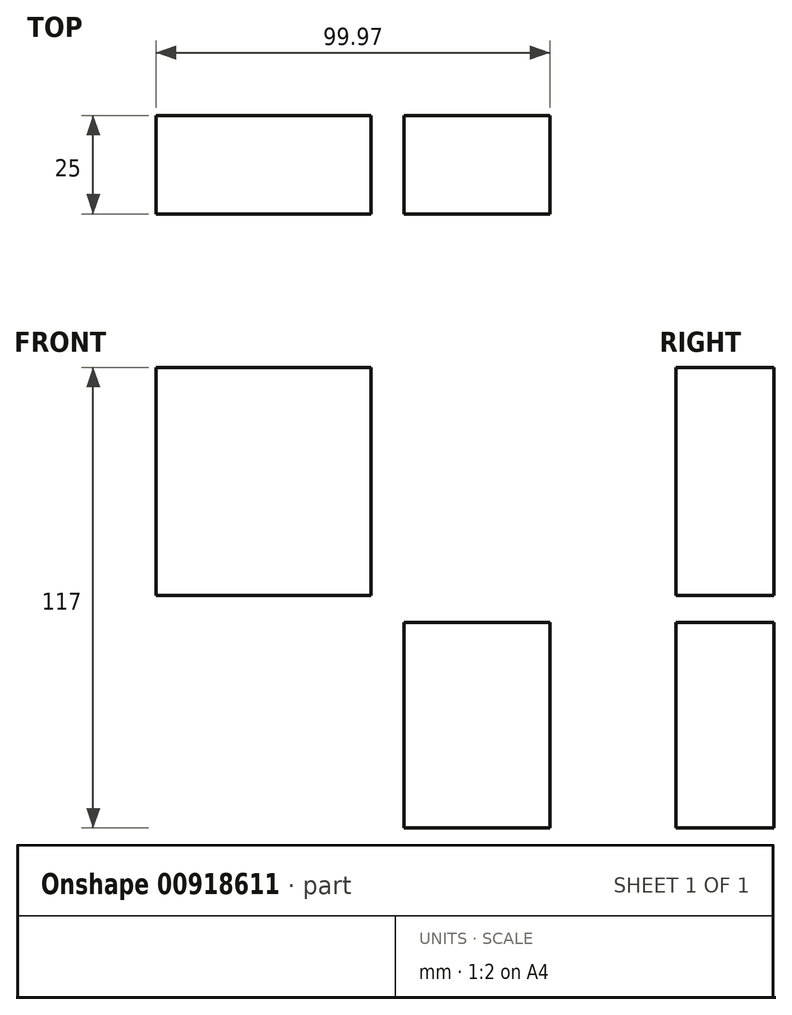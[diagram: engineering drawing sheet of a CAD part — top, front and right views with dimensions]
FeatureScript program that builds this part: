
annotation { "Feature Type Name" : "Feature", "Feature Type Description" : "" }
export const myFeature = defineFeature(function(context is Context, id is Id, definition is map)
    precondition{}
    {
        {
            var Q0;
            Q0=qCreatedBy(makeId("Front.planeOp"),FACE);
            var sketch = newSketch(context, id + "F0", { "sketchPlane" : qUnion([Q0])});
            skLineSegment(sketch, "E0.bottom", {"start": v(-133.56, 5.75) * mm, "end": v(-79.03, 5.75) * mm});
            skLineSegment(sketch, "E0.top", {"start": v(-133.56, 63.68) * mm, "end": v(-79.03, 63.68) * mm});
            skLineSegment(sketch, "E0.left", {"start": v(-133.56, 5.75) * mm, "end": v(-133.56, 63.68) * mm});
            skLineSegment(sketch, "E0.right", {"start": v(-79.03, 5.75) * mm, "end": v(-79.03, 63.68) * mm});
            skPoint(sketch, "E0.middle", {"position": v(-106.3, 34.71) * mm});
            skLineSegment(sketch, "E1.bottom", {"start": v(-70.6, -53.32) * mm, "end": v(-33.6, -53.32) * mm});
            skLineSegment(sketch, "E1.top", {"start": v(-70.6, -1.1) * mm, "end": v(-33.6, -1.1) * mm});
            skLineSegment(sketch, "E1.left", {"start": v(-70.6, -53.32) * mm, "end": v(-70.6, -1.1) * mm});
            skLineSegment(sketch, "E1.right", {"start": v(-33.6, -53.32) * mm, "end": v(-33.6, -1.1) * mm});
            skPoint(sketch, "E1.middle", {"position": v(-52.1, -27.2) * mm});
            skSolve(sketch);
        }
        {
            var Q0;
            Q0=makeQuery(id+"F0.imprint","IMPRINT",FACE,{"disambiguationData":[TD([[makeQuery(id+"F0.imprint","IMPRINT",EDGE,{"derivedFrom":sQuery(id+"F0.wireOp",EDGE,"E1.bottom")}),1.0]])]});
            var Q1;
            Q1=makeQuery(id+"F0.imprint","IMPRINT",FACE,{"disambiguationData":[TD([[makeQuery(id+"F0.imprint","IMPRINT",EDGE,{"derivedFrom":sQuery(id+"F0.wireOp",EDGE,"E0.bottom")}),1.0]])]});
            extrude(context, id + "F1", {"entities" : qUnion([Q0, Q1]), "depth" : 25 * mm, "offsetDistance" : 25 * mm});
        }
    });
